# Revit family: 81909001
name_source: partatom
category: Plumbing Fixtures
revit_build: Autodesk Revit 2018 (Build: 20170223_1515(x64)
units: mm (PartAtom-declared; Revit-internal decimal feet)

## family parameters
Always vertical = Yes
Cut with Voids When Loaded = No
OmniClass Number = 23.45.55.00
OmniClass Title = Sanitary Faucets, Wastes
Part Type = Normal
Room Calculation Point = No
Round Connector Dimension = Use Diameter
Shared = No
Work Plane-Based = No

## types (1)
- 81909001 Cover part for shower faucet, 3 V
    2D/3D/BIM Files URL = http://static.hansa.com
    3D View = https://static.hansa.com
    Advanced Features = Software settings adjustable via magnetic key
    Afterflow Period = 3 s (1/2/3/4/5/6/7/8/9/10 s)
    Approval ABP = PA-IX 29283/IBB
    AssetType = Fixed
    Automatic Flush Frequency = off (off/6/12/18/24/30/36/48/60/72 h)
    Automatic Flush Period = 30 s (30/60/90/120/180/240/300/360/480/600 s)
    BIMObjectName = 81909001
    Backflow Prevention EN1717 = EB
    Battery = AA 1.5 V Lithium x 2
    BodyMaterial = Brass
    Brand = HANSA
    Catalog Drawing URL = http://static.hansa.com
    Category = Bathroom;Shower;Public & Semi-public
    CloseOffRating = 0
    Color = Chrome
    Concealed Parts = Round rosette;BLUECLICK for an easy, screwless trim plate installation
    Dimension Drawing URL = http://static.hansa.com
    DurationUnit = Year
    EAN Number = 4057304004865
    EMC Directive = 2014/30/EU , 2011/65/EU
    EN Standard = EN 1111 , EN 15091
    ETIM Class Number = EC011327 Built-in mixing tap
    Electronic Parts = Autofocus infrared sensor;Solenoid valve;External control unit;Light indicated function(s);Low battery indicator
    FDV Document URL = http://www.hansa.com
    FaucetMainMaterial = Brass
    Features = Trim Kit;Thermostatic;Touchless;Battery-operated
    Finish = Polished
    Flow Drawing URL = http://static.hansa.com
    Flow Rate At 300kPa = 0.2 L/s
    FlowCoefficient = 0
    Group = Shower faucet
    IfcExportAs = IfcValveType
    IfcExportType = FAUCET
    Installation Type = Concealed wall mounting
    Installation and Maintenance Guide URL = http://static.hansa.com
    Interactive AR View URL = https://static.hansa.com
    Lever Handle = Temperature control handle
    Manufacturer = HANSA
    ManufacturerName = HANSA
    ManufacturerURL = http://www.hansa.com
    Market = International;Germany;Austria;Belgium;Netherlands;France;Czech Republic;Slovakia;Italy;Spain
    Material = Brass
    Max Flow Period = 60 s (10/30/60/90/120/150/180/210/240/300 s)
    Max. Hot Water Supply = 70 °C
    Mechanical Parts = Thermostatic cartridge for automatic temperature control;Non-return valve(s)
    Mobile Product Information URL = http://mpi.hansa.com
    Model = 81909001 Cover part for shower faucet, 3 V
    ModelReference = 81909001
    NBSDescription = Water supply fittings for baths
    NBSReference = 45-35-70/315
    Name = 81909001 Cover part for shower faucet, 3 V
    Name_en = 81909001 Cover part for shower faucet, 3 V
    Noise Class = I (ISO 3822)
    NominalDepth = 87 mm  [stored 0.285433 ft]
    NominalHeight = 170 mm  [stored 0.557743 ft]
    NominalWidth = 170 mm  [stored 0.557743 ft]
    Operating Distance = 10-500 mm (100/300/400/500/600 mm)
    Operating Voltage = 3 V
    Product Code = 81909001
    Product Family = HANSAELECTRA
    Product Image URL = http://static.hansa.com
    Product URL = http://static.hansa.com
    Protection Class = IP 55
    Revision = 3
    Sales Package dimensions (LxWxH) = 125 x 85 x 140
    Shape = Sculptured
    Size = 170x170x90 mm
    Spare-Part Information URL = http://static.hansa.com
    Surface treatment = Chrome
    Technical DataSheet URL = http://www.hansa.com
    Temperature = Temperature limiter;Thermostatic safety stop at 38°C
    Temperature Adjustments = Limitation option for maximum temperature and flow-rate ;Safety stop against scalding at 38°C
    UNSPSC Class Number = 30181810 Faucet trim
    URL ABP = http://static.hansa.com
    URL Declaration of Conformity = http://static.hansa.com
    URL REACH = http://static.hansa.com
    URL UN38.3 = http://www.hansa.com
    URL WEEE = http://www.hansa.com
    Uniclass2 = Pr_40_30_96_10
    Uniclass2015Description = Bath thermostatic water supply sets
    Uniclass2015Reference = Pr_40_20_87_10
    Version = 3
    VersionDate = 01/07/2022
    Warranty Information URL = http://warranty.hansa.com
    WarrantyDescription = http://warranty.hansa.com
    WarrantyDurationUnit = Year
    Working Pressure = 100 - 1000 kPa
    WorkingPressure = 100 - 1000 kPa

note: [stored X ft] marks values corroborated as IEEE doubles in the binary element streams (Revit-internal decimal feet)

## geometry (parser evidence)
native form markers: Sweep x5
no freeform markers — native parametric forms only
